# Revit family: VLN_Aqua_B9315_BIM_NL
name_source: partatom
category: Plumbing Fixtures
revit_build: Autodesk Revit MEP 2014 (Build: 20130308_1515(x64)
units: mm (PartAtom-declared; Revit-internal decimal feet)

## types (1)
- B9315AA - AQUA M1 SHK 1F/80 600MM MET/1500 VLN
    Accessories = www.idealstandardnederland.nl
    AreaUnits = millimeters
    Assembly Code = C1030200
    AssetType = Vast
    BIMObjectName = VLN_Venlo_ShowerFittingsPackage_B9315AA
    BREEAMApproved = No
    BarCode = 3800861023531
    Brand = Venlo
    CWFU = 0
    Color = Chroom
    ConnectionType = Sanitair
    Cost = 0 $
    Default Elevation = 800 mm
    Description = Venlo Aqua 80 glijstangcombinatie 600 mm. Handdouche 1 functie. Glijstang 600 mm en doucheslang "Metalflex" 1500 mm. 8 l/min bij 3 bar.
    DurationUnit = jaar
    ECA = No
    ExpectedLife = 25
    Features = Glijstangcombinatie 600 mm. Handdouche 1 functie. Glijstang 600 mm en doucheslang "Metalflex" 1500 mm. 8 l/min bij 3 bar.
    Finish = Chroom
    HWFU = 0
    IfcExportAs = IfcValveType
    IfcExportType = FAUCET
    InstallationInstructions = http://www.idealstandardnederland.nl
    LinearUnits = millimeters
    ManufacturerURL = www.idealstandardnederland.nl
    Material = Messing
    Model = B9315AA
    ModelNumber = B9315AA
    ModelReference = Venlo Aqua 80 glijstangcombinatie 600 mm. Handdouche 1 functie. Glijstang 600 mm en doucheslang "Metalflex" 1500 mm. 8 l/min bij 3 bar.
    NBSDescription = Shower fittings package
    NBSReference = 45-35-70/330
    Name = ShowerFittingsPackage_B9315AA_Venlo
    NettWeight = 1.152 kg
    NominalHeight = 614 mm
    NominalLength = 137 mm
    NominalWidth = 151 mm
    ProductInformation = http://www.idealstandardnederland.nl
    Shape = Gesculptuurd
    Size = 151 x 137 x 614 mm
    Space = Internal
    SpareParts = www.idealstandardnederland.nl
    TMV3 = Yes
    TestPressure = 10 Bar
    URL = www.idealstandardnederland.nl
    Uniclass2015Code = Pr_40_20_87_75
    Uniclass2015Title = Shower fittings package
    Uniclass2015Version = Products v1.1
    Version = 1
    VolumeUnits = liter
    WFU = 0
    WRAS = No
    WarrantyDescription = Fabrieksgarantie
    WarrantyDurationParts = 5
    WarrantyDurationUnit = jaar
    WaterEfficientProduct = No
    WorkingPressure = 1-5 bar

## geometry (parser evidence)
native form markers: Sweep x2
no freeform markers — native parametric forms only
